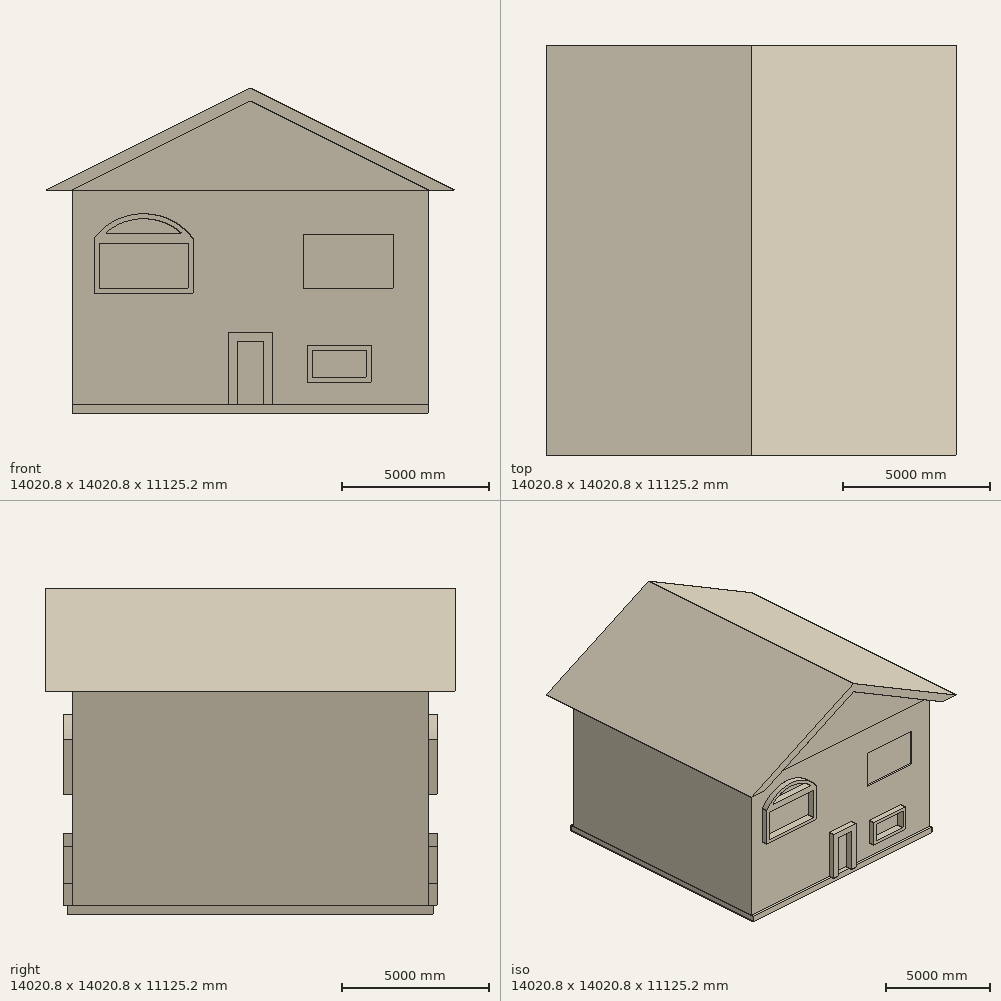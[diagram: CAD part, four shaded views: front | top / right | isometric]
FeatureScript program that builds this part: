
annotation { "Feature Type Name" : "Feature", "Feature Type Description" : "" }
export const myFeature = defineFeature(function(context is Context, id is Id, definition is map)
    precondition{}
    {
        {
            var Q0;
            Q0=qCreatedBy(makeId("Front.planeOp"),FACE);
            var sketch = newSketch(context, id + "F0", { "sketchPlane" : qUnion([Q0])});
            skLineSegment(sketch, "E0", {"start": v(0, 0) * mm, "end": v(-6096, 0) * mm});
            skLineSegment(sketch, "E1", {"start": v(0, 0) * mm, "end": v(6096, 0) * mm});
            skLineSegment(sketch, "E2", {"start": v(0, 0) * mm, "end": v(0, 3048) * mm, "construction": true});
            skLineSegment(sketch, "E3", {"start": v(0, 3048) * mm, "end": v(-6096, 0) * mm});
            skLineSegment(sketch, "E4", {"start": v(0, 3048) * mm, "end": v(6096, 0) * mm});
            skLineSegment(sketch, "E5", {"start": v(-6096, 0) * mm, "end": v(-7010.4, 0) * mm});
            skLineSegment(sketch, "E6", {"start": v(6096, 0) * mm, "end": v(7010.4, 0) * mm});
            skLineSegment(sketch, "E7", {"start": v(0, 3048) * mm, "end": v(0, 3505.2) * mm});
            skLineSegment(sketch, "E8", {"start": v(0, 3505.2) * mm, "end": v(7010.4, 0) * mm});
            skLineSegment(sketch, "E9", {"start": v(0, 3505.2) * mm, "end": v(-7010.4, 0) * mm});
            skLineSegment(sketch, "E10", {"start": v(-6096, 0) * mm, "end": v(-6096, -7315.2) * mm});
            skLineSegment(sketch, "E11", {"start": v(6096, 0) * mm, "end": v(6096, -7315.2) * mm});
            skLineSegment(sketch, "E12", {"start": v(6096, -7315.2) * mm, "end": v(-6096, -7315.2) * mm});
            skLineSegment(sketch, "E13", {"start": v(-6096, -7315.2) * mm, "end": v(-6096, -7620) * mm});
            skLineSegment(sketch, "E14", {"start": v(-6096, -7620) * mm, "end": v(6096, -7620) * mm});
            skLineSegment(sketch, "E15", {"start": v(6096, -7315.2) * mm, "end": v(6096, -7620) * mm});
            skLineSegment(sketch, "E16", {"start": v(0, 0) * mm, "end": v(0, -7315.2) * mm, "construction": true});
            skLineSegment(sketch, "E17", {"start": v(-457.2, -7315.2) * mm, "end": v(-457.2, -5181.6) * mm});
            skLineSegment(sketch, "E18", {"start": v(-457.2, -5181.6) * mm, "end": v(457.2, -5181.6) * mm});
            skLineSegment(sketch, "E19", {"start": v(457.2, -5181.6) * mm, "end": v(457.2, -7315.2) * mm});
            skLineSegment(sketch, "E20.bottom", {"start": v(2133.6, -5486.4) * mm, "end": v(3962.4, -5486.4) * mm});
            skLineSegment(sketch, "E20.top", {"start": v(2133.6, -6400.8) * mm, "end": v(3962.4, -6400.8) * mm});
            skLineSegment(sketch, "E20.left", {"start": v(2133.6, -5486.4) * mm, "end": v(2133.6, -6400.8) * mm});
            skLineSegment(sketch, "E20.right", {"start": v(3962.4, -5486.4) * mm, "end": v(3962.4, -6400.8) * mm});
            skLineSegment(sketch, "E21.0", {"start": v(1962.91, -5315.71) * mm, "end": v(4133.09, -5315.71) * mm});
            skLineSegment(sketch, "E21.1", {"start": v(1962.91, -5315.71) * mm, "end": v(1962.91, -6571.49) * mm});
            skLineSegment(sketch, "E21.2", {"start": v(1962.91, -6571.49) * mm, "end": v(4133.09, -6571.49) * mm});
            skLineSegment(sketch, "E21.3", {"start": v(4133.09, -5315.71) * mm, "end": v(4133.09, -6571.49) * mm});
            skLineSegment(sketch, "E22.bottom", {"start": v(1828.8, -1524) * mm, "end": v(4876.8, -1524) * mm});
            skLineSegment(sketch, "E22.top", {"start": v(1828.8, -3352.8) * mm, "end": v(4876.8, -3352.8) * mm});
            skLineSegment(sketch, "E22.left", {"start": v(1828.8, -1524) * mm, "end": v(1828.8, -3352.8) * mm});
            skLineSegment(sketch, "E22.right", {"start": v(4876.8, -1524) * mm, "end": v(4876.8, -3352.8) * mm});
            skLineSegment(sketch, "E23.bottom", {"start": v(-5175.84, -1828.8) * mm, "end": v(-2127.84, -1828.8) * mm});
            skLineSegment(sketch, "E23.top", {"start": v(-5175.84, -3352.8) * mm, "end": v(-2127.84, -3352.8) * mm});
            skLineSegment(sketch, "E23.left", {"start": v(-5175.84, -1828.8) * mm, "end": v(-5175.84, -3352.8) * mm});
            skLineSegment(sketch, "E23.right", {"start": v(-2127.84, -1828.8) * mm, "end": v(-2127.84, -3352.8) * mm});
            skLineSegment(sketch, "E24.0", {"start": v(-5346.53, -1658.11) * mm, "end": v(-5346.53, -3523.49) * mm});
            skLineSegment(sketch, "E24.1", {"start": v(-5346.53, -1658.11) * mm, "end": v(-1957.16, -1658.11) * mm});
            skLineSegment(sketch, "E24.2", {"start": v(-1957.16, -1658.11) * mm, "end": v(-1957.16, -3523.49) * mm});
            skLineSegment(sketch, "E24.3", {"start": v(-5346.53, -3523.49) * mm, "end": v(-1957.16, -3523.49) * mm});
            skArc(sketch, "E25", {"start": v(-1957.16, -1658.11) * mm, "mid": v(-3651.84, -799.67) * mm, "end": v(-5346.53, -1658.11) * mm});
            skArc(sketch, "E26.0", {"start": v(-2336.6, -1487.42) * mm, "mid": v(-3651.84, -970.36) * mm, "end": v(-4967.1, -1487.42) * mm});
            skLineSegment(sketch, "E26.1", {"start": v(-4967.1, -1487.42) * mm, "end": v(-2336.6, -1487.42) * mm});
            skLineSegment(sketch, "E27.0", {"start": v(762, -4876.8) * mm, "end": v(762, -7315.2) * mm});
            skLineSegment(sketch, "E27.1", {"start": v(-762, -4876.8) * mm, "end": v(762, -4876.8) * mm});
            skLineSegment(sketch, "E27.2", {"start": v(-762, -7315.2) * mm, "end": v(-762, -4876.8) * mm});
            skSolve(sketch);
        }
        {
            var Q0;
            Q0=makeQuery(id+"F0.imprint","IMPRINT",FACE,{"disambiguationData":[TD([[makeQuery(id+"F0.imprint","IMPRINT",EDGE,{"derivedFrom":sQuery(id+"F0.wireOp",EDGE,"E3")}),-1.0]])]});
            var Q1;
            Q1=makeQuery(id+"F0.imprint","IMPRINT",FACE,{"disambiguationData":[TD([[makeQuery(id+"F0.imprint","IMPRINT",EDGE,{"derivedFrom":sQuery(id+"F0.wireOp",EDGE,"E4")}),1.0]])]});
            extrude(context, id + "F1", {"entities" : qUnion([Q0, Q1]), "endBound" : BoundingType.SYMMETRIC, "depth" : 14020.8 * mm, "offsetDistance" : 30.48 * mm});
        }
        {
            var Q0;
            Q0=makeQuery(id+"F0.imprint","IMPRINT",FACE,{"disambiguationData":[TD([[makeQuery(id+"F0.imprint","IMPRINT",EDGE,{"derivedFrom":sQuery(id+"F0.wireOp",EDGE,"E0")}),-1.0]])]});
            extrude(context, id + "F2", {"entities" : qUnion([Q0]), "operationType" : NewBodyOperationType.ADD, "endBound" : BoundingType.SYMMETRIC, "depth" : 12496.8 * mm, "offsetDistance" : 30.48 * mm});
        }
        {
            var Q0;
            {var subQ6=sQuery(id+"F0.wireOp",EDGE,"E13");Q0=makeQuery(id+"F0.imprint","IMPRINT",FACE,{"disambiguationData":[TD([[makeQuery(id+"F0.imprint","IMPRINT",EDGE,{"derivedFrom":subQ6}),1.0]])]});}
            extrude(context, id + "F3", {"entities" : qUnion([Q0]), "endBound" : BoundingType.SYMMETRIC, "depth" : 12496.8 * mm, "offsetDistance" : 30.48 * mm});
        }
        {
            var Q0;
            Q0=makeQuery(id+"F0.imprint","IMPRINT",FACE,{"disambiguationData":[TD([[makeQuery(id+"F0.imprint","IMPRINT",EDGE,{"derivedFrom":sQuery(id+"F0.wireOp",EDGE,"E0")}),1.0]])]});
            extrude(context, id + "F4", {"entities" : qUnion([Q0]), "endBound" : BoundingType.SYMMETRIC, "depth" : 12192 * mm, "offsetDistance" : 30.48 * mm});
        }
        {
            var Q0;
            Q0=makeQuery(id+"F0.imprint","IMPRINT",FACE,{"disambiguationData":[TD([[makeQuery(id+"F0.imprint","IMPRINT",EDGE,{"derivedFrom":sQuery(id+"F0.wireOp",EDGE,"E23.bottom")}),-1.0]])]});
            var Q1;
            Q1=makeQuery(id+"F0.imprint","IMPRINT",FACE,{"disambiguationData":[TD([[makeQuery(id+"F0.imprint","IMPRINT",EDGE,{"derivedFrom":sQuery(id+"F0.wireOp",EDGE,"E22.bottom")}),-1.0]])]});
            var Q2;
            Q2=makeQuery(id+"F0.imprint","IMPRINT",FACE,{"disambiguationData":[TD([[makeQuery(id+"F0.imprint","IMPRINT",EDGE,{"derivedFrom":sQuery(id+"F0.wireOp",EDGE,"E20.bottom")}),-1.0]])]});
            var Q3;
            {var subQ0=sQuery(id+"F0.wireOp",EDGE,"E17");Q3=makeQuery(id+"F0.imprint","IMPRINT",FACE,{"disambiguationData":[TD([[makeQuery(id+"F0.imprint","IMPRINT",EDGE,{"derivedFrom":subQ0}),-1.0]])]});}
            var Q4;
            Q4=makeQuery(id+"F0.imprint","IMPRINT",FACE,{"disambiguationData":[TD([[makeQuery(id+"F0.imprint","IMPRINT",EDGE,{"derivedFrom":sQuery(id+"F0.wireOp",EDGE,"E26.0")}),1.0]])]});
            extrude(context, id + "F5", {"entities" : qUnion([Q0, Q1, Q2, Q3, Q4]), "endBound" : BoundingType.SYMMETRIC, "depth" : 12039.6 * mm, "offsetDistance" : 30.48 * mm});
        }
        {
            var Q0;
            Q0=makeQuery(id+"F0.imprint","IMPRINT",FACE,{"disambiguationData":[TD([[makeQuery(id+"F0.imprint","IMPRINT",EDGE,{"derivedFrom":sQuery(id+"F0.wireOp",EDGE,"E23.bottom")}),1.0]])]});
            var Q1;
            Q1=makeQuery(id+"F0.imprint","IMPRINT",FACE,{"disambiguationData":[TD([[makeQuery(id+"F0.imprint","IMPRINT",EDGE,{"derivedFrom":sQuery(id+"F0.wireOp",EDGE,"E24.1")}),1.0]])]});
            var Q2;
            Q2=makeQuery(id+"F0.imprint","IMPRINT",FACE,{"disambiguationData":[TD([[makeQuery(id+"F0.imprint","IMPRINT",EDGE,{"derivedFrom":sQuery(id+"F0.wireOp",EDGE,"E20.bottom")}),1.0]])]});
            var Q3;
            {var subQ0=sQuery(id+"F0.wireOp",EDGE,"E17");Q3=makeQuery(id+"F0.imprint","IMPRINT",FACE,{"disambiguationData":[TD([[makeQuery(id+"F0.imprint","IMPRINT",EDGE,{"derivedFrom":subQ0}),1.0]])]});}
            extrude(context, id + "F6", {"entities" : qUnion([Q0, Q1, Q2, Q3]), "endBound" : BoundingType.SYMMETRIC, "depth" : 12801.6 * mm, "offsetDistance" : 30.48 * mm});
        }
    });
